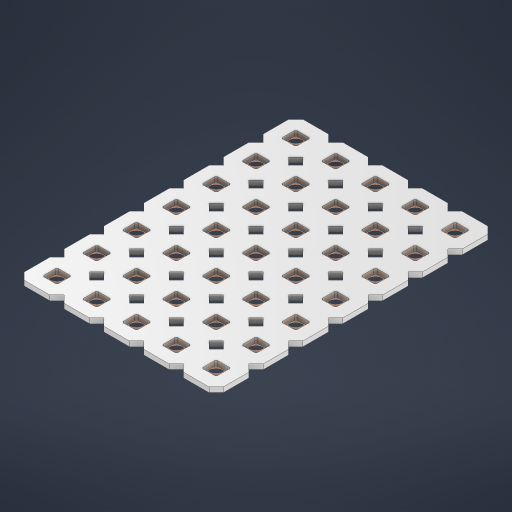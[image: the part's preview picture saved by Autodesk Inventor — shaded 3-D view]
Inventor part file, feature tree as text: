
AUTODESK INVENTOR PART (.ipt)
format: ipt  version: 2024 (Build 280153000, 153)  size: 676,352 bytes
history: native  units: in
note: dims shown in document units (in); Inventor stores cm internally (conversion verified against a paired STEP export)
features: other x36, extrude x34, pattern_linear x1
ambient origin geometry x8: Origin, YZ Plane, XZ Plane, XY Plane, X Axis, Y Axis, Z Axis, Center Point
bodies: Solid1 (feature_tree), Body (feature_tree)
feature tree (71):
  pattern_linear  "Rectangular Pattern1"  Spacing1=0.5in  [1 undecoded]
  other  "Srf1"
  other  "Srf126"
  other  "Srf127"
  other  "Srf128"
  other  "Srf129"
  other  "Srf130"
  other  "Srf131"
  other  "Srf268"
  other  "Srf269"
  other  "Srf270"
  other  "Srf271"
  other  "Srf272"
  other  "Srf273"
  other  "Srf274"
  other  "Srf293"
  other  "Srf294"
  other  "Srf295"
  other  "Srf296"
  other  "Srf297"
  other  "Srf298"
  other  "Srf299"
  other  "Srf318"
  other  "Srf319"
  other  "Srf320"
  other  "Srf321"
  other  "Srf322"
  other  "Srf323"
  other  "Srf324"
  other  "Srf343"
  other  "Srf344"
  other  "Srf345"
  other  "Srf346"
  other  "Srf347"
  other  "Srf348"
  other  "Srf349"
  other  "Circle"
  extrude  "ExtrusionSrf126"  Depth=0.182in
  extrude  "ExtrusionSrf127"  Depth=0.09in
  extrude  "ExtrusionSrf128"  Depth=0.09in
  extrude  "ExtrusionSrf129"  Depth=0.09in
  extrude  "ExtrusionSrf130"  Depth=0.09in
  extrude  "ExtrusionSrf131"  Depth=0.09in
  extrude  "ExtrusionSrf268"  Depth=0.09in
  extrude  "ExtrusionSrf269"  Depth=0.09in
  extrude  "ExtrusionSrf270"  Depth=0.09in
  extrude  "ExtrusionSrf271"  Depth=0.02in
  extrude  "ExtrusionSrf272"  TaperAngle=0.0deg  [1 undecoded]
  extrude  "ExtrusionSrf273"  Depth=0.172in
  extrude  "ExtrusionSrf274"  Depth=0.0625in TaperAngle=0.0deg
  extrude  "ExtrusionSrf293"  Depth=0.5in
  extrude  "ExtrusionSrf294"  Depth=0.5in
  extrude  "ExtrusionSrf295"  [1 undecoded]
  extrude  "ExtrusionSrf296"  [1 undecoded]
  extrude  "ExtrusionSrf297"  [1 undecoded]
  extrude  "ExtrusionSrf298"  [1 undecoded]
  extrude  "ExtrusionSrf299"  [1 undecoded]
  extrude  "ExtrusionSrf318"  [1 undecoded]
  extrude  "ExtrusionSrf319"  [1 undecoded]
  extrude  "ExtrusionSrf320"  [1 undecoded]
  extrude  "ExtrusionSrf321"  [1 undecoded]
  extrude  "ExtrusionSrf322"  [1 undecoded]
  extrude  "ExtrusionSrf323"  [1 undecoded]
  extrude  "ExtrusionSrf324"  [1 undecoded]
  extrude  "ExtrusionSrf343"  [1 undecoded]
  extrude  "ExtrusionSrf344"  [1 undecoded]
  extrude  "ExtrusionSrf345"  [1 undecoded]
  extrude  "ExtrusionSrf346"  [1 undecoded]
  extrude  "ExtrusionSrf347"  [1 undecoded]
  extrude  "ExtrusionSrf348"  [1 undecoded]
  extrude  "ExtrusionSrf349"  [1 undecoded]
note: 21 required parameter values undecoded (feature->parameter linkage not recoverable at this tier; creation-order binding heuristic only, values carry confidence <= 0.55)
